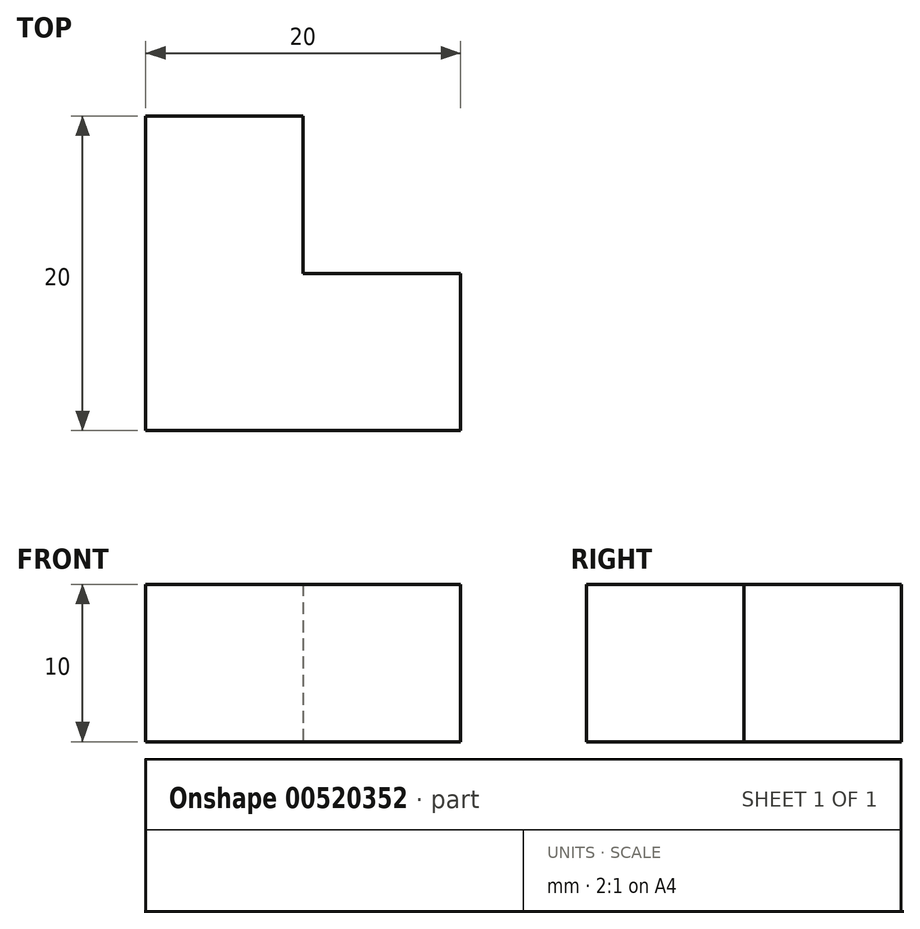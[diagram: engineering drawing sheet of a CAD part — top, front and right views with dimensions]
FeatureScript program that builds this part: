
annotation { "Feature Type Name" : "Feature", "Feature Type Description" : "" }
export const myFeature = defineFeature(function(context is Context, id is Id, definition is map)
    precondition{}
    {
        {
            var Q0;
            Q0=qCreatedBy(makeId("Top.planeOp"),FACE);
            var sketch = newSketch(context, id + "F0", { "sketchPlane" : qUnion([Q0])});
            skLineSegment(sketch, "E0", {"start": v(-53.29, 30.23) * mm, "end": v(-53.29, 10.23) * mm});
            skLineSegment(sketch, "E1", {"start": v(-53.29, 10.23) * mm, "end": v(-33.29, 10.23) * mm});
            skLineSegment(sketch, "E2", {"start": v(-33.29, 10.23) * mm, "end": v(-33.29, 20.23) * mm});
            skLineSegment(sketch, "E3", {"start": v(-43.29, 20.23) * mm, "end": v(-33.29, 20.23) * mm});
            skLineSegment(sketch, "E4", {"start": v(-43.29, 20.23) * mm, "end": v(-43.29, 30.23) * mm});
            skLineSegment(sketch, "E5", {"start": v(-53.29, 30.23) * mm, "end": v(-43.29, 30.23) * mm});
            skSolve(sketch);
        }
        {
            var Q0;
            Q0=makeQuery(id+"F0.imprint","IMPRINT",FACE,{"disambiguationData":[TD([[makeQuery(id+"F0.imprint","IMPRINT",EDGE,{"derivedFrom":sQuery(id+"F0.wireOp",EDGE,"E0")}),1.0]])]});
            extrude(context, id + "F1", {"entities" : qUnion([Q0]), "depth" : 10 * mm, "offsetDistance" : 25 * mm});
        }
    });
